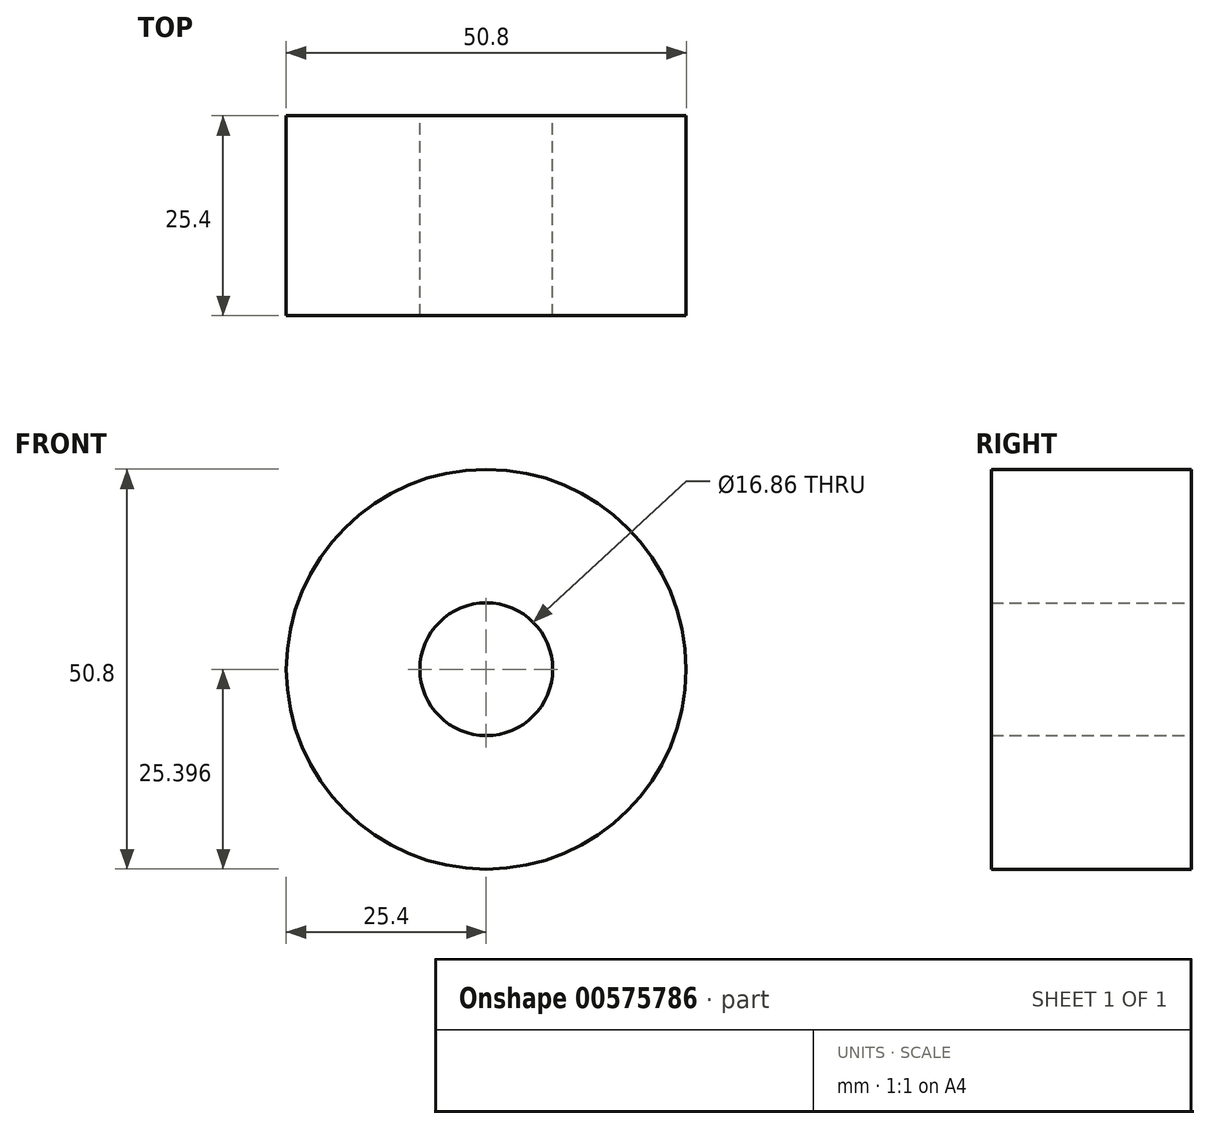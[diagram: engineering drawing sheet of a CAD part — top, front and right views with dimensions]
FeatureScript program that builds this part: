
annotation { "Feature Type Name" : "Feature", "Feature Type Description" : "" }
export const myFeature = defineFeature(function(context is Context, id is Id, definition is map)
    precondition{}
    {
        {
            var Q0;
            Q0=qCreatedBy(makeId("Front.planeOp"),FACE);
            var sketch = newSketch(context, id + "F0", { "sketchPlane" : qUnion([Q0])});
            skCircle(sketch, "E0", {"center": v(-33.86, 34.9) * mm, "radius": 25.4 * mm});
            skSolve(sketch);
        }
        {
            var Q0;
            Q0 = qSketchRegion(id + "F0", true);
            extrude(context, id + "F1", {"entities" : qUnion([Q0]), "depth" : 25.4 * mm, "offsetDistance" : 25.4 * mm});
        }
        {
            var Q0;
            Q0=makeQuery(id+"F1.opExtrude","CAP_FACE",FACE,{"disambiguationData":[OSD([sQuery(id+"F0.wireOp",EDGE,"E0")])],"isStart":true});
            var sketch = newSketch(context, id + "F2", { "sketchPlane" : qUnion([Q0])});
            skCircle(sketch, "E1", {"center": v(33.86, 34.9) * mm, "radius": 8.43 * mm});
            skSolve(sketch);
        }
        {
            var Q0;
            Q0=makeQuery(id+"F2.imprint","IMPRINT",FACE,{"disambiguationData":[TD([[makeQuery(id+"F2.imprint","IMPRINT",EDGE,{"derivedFrom":sQuery(id+"F2.wireOp",EDGE,"E1")}),1.0]])]});
            extrude(context, id + "F3", {"entities" : qUnion([Q0]), "operationType" : NewBodyOperationType.REMOVE, "oppositeDirection" : true, "depth" : 25.4 * mm, "offsetDistance" : 25.4 * mm});
        }
    });
